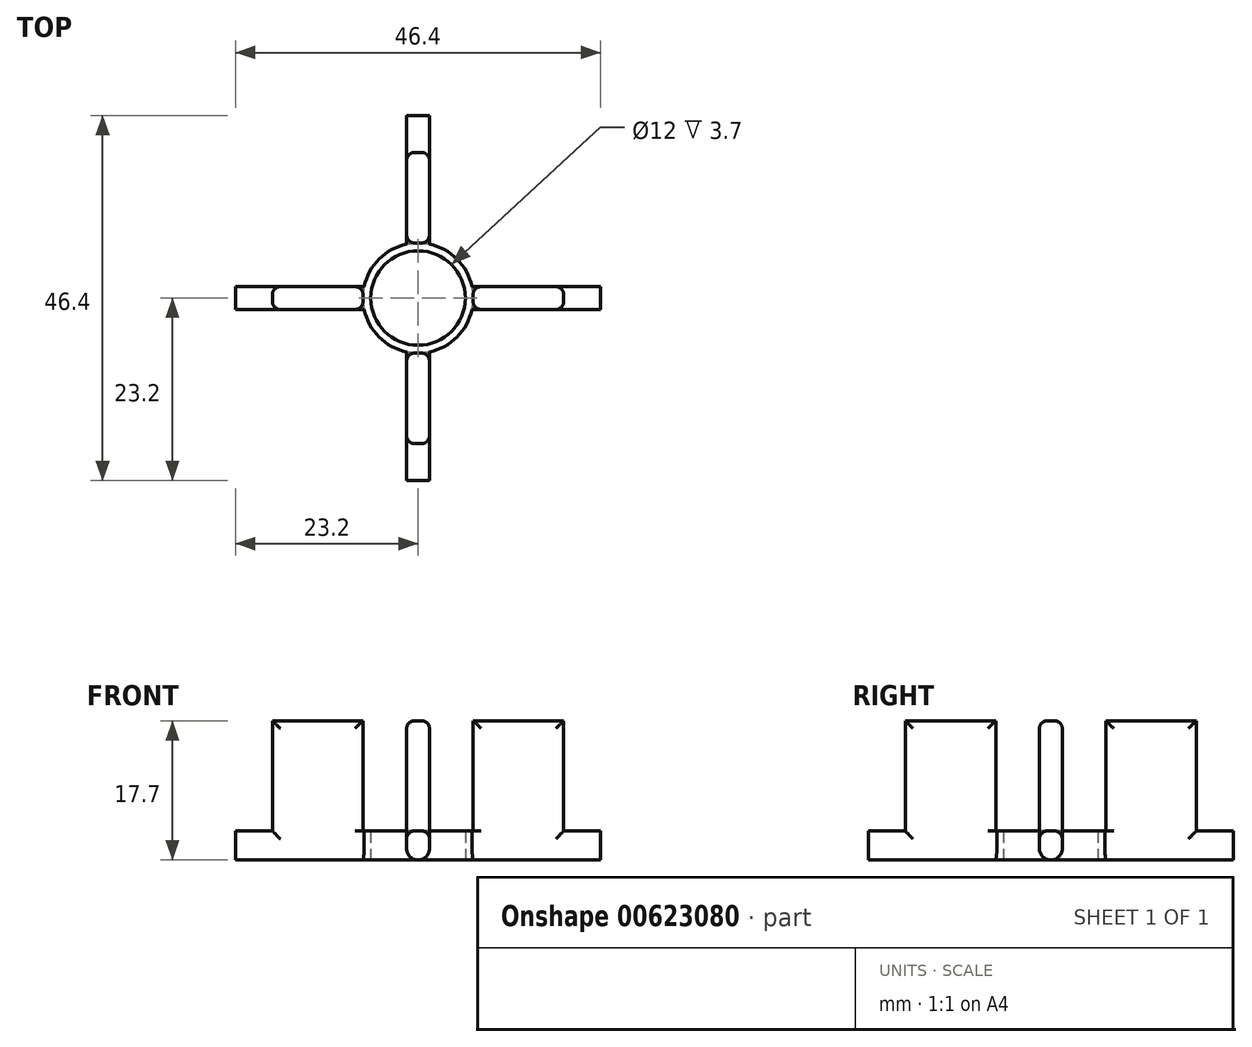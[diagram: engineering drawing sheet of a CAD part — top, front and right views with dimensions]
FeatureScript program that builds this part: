
annotation { "Feature Type Name" : "Feature", "Feature Type Description" : "" }
export const myFeature = defineFeature(function(context is Context, id is Id, definition is map)
    precondition{}
    {
        {
            var Q0;
            Q0=qCreatedBy(makeId("Top.planeOp"),FACE);
            var sketch = newSketch(context, id + "F0", { "sketchPlane" : qUnion([Q0])});
            skCircle(sketch, "E0", {"center": v(0, 0) * mm, "radius": 6 * mm});
            skCircle(sketch, "E1", {"center": v(0, 0) * mm, "radius": 7 * mm});
            skLineSegment(sketch, "E2", {"start": v(-7, 0) * mm, "end": v(-23.2, 0) * mm});
            skLineSegment(sketch, "E3", {"start": v(-23.2, -1.45) * mm, "end": v(-6.85, -1.45) * mm});
            skLineSegment(sketch, "E4", {"start": v(-23.2, -1.45) * mm, "end": v(-23.2, 1.45) * mm});
            skLineSegment(sketch, "E5", {"start": v(-23.2, 1.45) * mm, "end": v(-6.85, 1.45) * mm});
            skLineSegment(sketch, "E6", {"start": v(0, 7) * mm, "end": v(0, 23.2) * mm});
            skLineSegment(sketch, "E7", {"start": v(-1.45, 23.2) * mm, "end": v(-1.45, 6.85) * mm});
            skLineSegment(sketch, "E8", {"start": v(-1.45, 23.2) * mm, "end": v(1.45, 23.2) * mm});
            skLineSegment(sketch, "E9", {"start": v(1.45, 23.2) * mm, "end": v(1.45, 6.85) * mm});
            skLineSegment(sketch, "E10", {"start": v(7, 0) * mm, "end": v(23.2, 0) * mm});
            skLineSegment(sketch, "E11", {"start": v(23.2, 1.45) * mm, "end": v(6.85, 1.45) * mm});
            skLineSegment(sketch, "E12", {"start": v(23.2, 1.45) * mm, "end": v(23.2, -1.45) * mm});
            skLineSegment(sketch, "E13", {"start": v(23.2, -1.45) * mm, "end": v(6.85, -1.45) * mm});
            skLineSegment(sketch, "E14", {"start": v(0, -7) * mm, "end": v(0, -23.2) * mm});
            skLineSegment(sketch, "E15", {"start": v(-1.45, -23.2) * mm, "end": v(-1.45, -6.85) * mm});
            skLineSegment(sketch, "E16", {"start": v(-1.45, -23.2) * mm, "end": v(1.45, -23.2) * mm});
            skLineSegment(sketch, "E17", {"start": v(1.45, -23.2) * mm, "end": v(1.45, -6.85) * mm});
            skSolve(sketch);
        }
        {
            var Q0;
            Q0 = qSketchRegion(id + "F0", true);
            extrude(context, id + "F1", {"entities" : qUnion([Q0]), "depth" : 3.7 * mm, "offsetDistance" : 25 * mm});
        }
        {
            var Q0;
            Q0=makeQuery(id+"F1.opExtrude","CAP_EDGE",EDGE,{"disambiguationData":[OSD([sQuery(id+"F0.wireOp",EDGE,"E9")])],"isStart":true});
            var Q1;
            Q1=makeQuery(id+"F1.opExtrude","CAP_EDGE",EDGE,{"disambiguationData":[OSD([sQuery(id+"F0.wireOp",EDGE,"E11")])],"isStart":true});
            var Q2;
            Q2=makeQuery(id+"F1.opExtrude","CAP_EDGE",EDGE,{"disambiguationData":[OSD([sQuery(id+"F0.wireOp",EDGE,"E13")])],"isStart":true});
            var Q3;
            Q3=makeQuery(id+"F1.opExtrude","CAP_EDGE",EDGE,{"disambiguationData":[OSD([sQuery(id+"F0.wireOp",EDGE,"E17")])],"isStart":true});
            var Q4;
            Q4=makeQuery(id+"F1.opExtrude","CAP_EDGE",EDGE,{"disambiguationData":[OSD([sQuery(id+"F0.wireOp",EDGE,"E15")])],"isStart":true});
            var Q5;
            Q5=makeQuery(id+"F1.opExtrude","CAP_EDGE",EDGE,{"disambiguationData":[OSD([sQuery(id+"F0.wireOp",EDGE,"E3")])],"isStart":true});
            var Q6;
            Q6=makeQuery(id+"F1.opExtrude","CAP_EDGE",EDGE,{"disambiguationData":[OSD([sQuery(id+"F0.wireOp",EDGE,"E5")])],"isStart":true});
            var Q7;
            Q7=makeQuery(id+"F1.opExtrude","CAP_EDGE",EDGE,{"disambiguationData":[OSD([sQuery(id+"F0.wireOp",EDGE,"E7")])],"isStart":true});
            fillet(context, id + "F2", {"entities" : qUnion([Q0, Q1, Q2, Q3, Q4, Q5, Q6, Q7]), "radius" : 1.45 * mm, "tangentPropagation" : true, "allowEdgeOverflow" : false});
        }
        {
            var Q0;
            Q0=makeQuery(id+"F1.opExtrude","CAP_FACE",FACE,{"disambiguationData":[OSD([sQuery(id+"F0.wireOp",EDGE,"E0"),sQuery(id+"F0.wireOp",EDGE,"E1"),sQuery(id+"F0.wireOp",EDGE,"E3"),sQuery(id+"F0.wireOp",EDGE,"E4"),sQuery(id+"F0.wireOp",EDGE,"E5"),sQuery(id+"F0.wireOp",EDGE,"E7"),sQuery(id+"F0.wireOp",EDGE,"E8"),sQuery(id+"F0.wireOp",EDGE,"E9"),sQuery(id+"F0.wireOp",EDGE,"E11"),sQuery(id+"F0.wireOp",EDGE,"E12"),sQuery(id+"F0.wireOp",EDGE,"E13"),sQuery(id+"F0.wireOp",EDGE,"E15"),sQuery(id+"F0.wireOp",EDGE,"E16"),sQuery(id+"F0.wireOp",EDGE,"E17")])],"isStart":false});
            var sketch = newSketch(context, id + "F3", { "sketchPlane" : qUnion([Q0])});
            skArc(sketch, "E18", {"start": v(18.44, -1.45) * mm, "mid": v(18.5, 0) * mm, "end": v(18.44, 1.45) * mm});
            skLineSegment(sketch, "E19.bottom", {"start": v(18.44, -1.45) * mm, "end": v(6.85, -1.45) * mm});
            skLineSegment(sketch, "E19.top", {"start": v(18.44, 1.45) * mm, "end": v(6.85, 1.45) * mm});
            skLineSegment(sketch, "E19.left", {"start": v(18.44, -1.45) * mm, "end": v(18.44, 1.45) * mm});
            skLineSegment(sketch, "E19.right", {"start": v(-18.44, -1.45) * mm, "end": v(-18.44, 1.45) * mm});
            skLineSegment(sketch, "E20.bottom", {"start": v(1.45, -18.44) * mm, "end": v(-1.45, -18.44) * mm});
            skLineSegment(sketch, "E20.top", {"start": v(1.45, 18.44) * mm, "end": v(-1.45, 18.44) * mm});
            skLineSegment(sketch, "E20.left", {"start": v(1.45, -18.44) * mm, "end": v(1.45, -6.85) * mm});
            skLineSegment(sketch, "E20.right", {"start": v(-1.45, -18.44) * mm, "end": v(-1.45, -6.85) * mm});
            skLineSegment(sketch, "E21.trimOffspring", {"start": v(-6.85, -1.45) * mm, "end": v(-18.44, -1.45) * mm});
            skLineSegment(sketch, "E22.trimOffspring", {"start": v(1.45, 6.85) * mm, "end": v(1.45, 18.44) * mm});
            skLineSegment(sketch, "E23.trimOffspring", {"start": v(-1.45, 6.85) * mm, "end": v(-1.45, 18.44) * mm});
            skLineSegment(sketch, "E24.trimOffspring", {"start": v(-6.85, 1.45) * mm, "end": v(-18.44, 1.45) * mm});
            skArc(sketch, "E25.trimOffspring", {"start": v(-1.45, -18.44) * mm, "mid": v(0, -18.5) * mm, "end": v(1.45, -18.44) * mm});
            skArc(sketch, "E26.trimOffspring", {"start": v(-18.44, 1.45) * mm, "mid": v(-18.5, 0) * mm, "end": v(-18.44, -1.45) * mm});
            skArc(sketch, "E27.trimOffspring", {"start": v(1.45, 18.44) * mm, "mid": v(0, 18.5) * mm, "end": v(-1.45, 18.44) * mm});
            skArc(sketch, "E28", {"start": v(-1.45, -6.85) * mm, "mid": v(0, -7) * mm, "end": v(1.45, -6.85) * mm});
            skArc(sketch, "E29.trimOffspring", {"start": v(-6.85, 1.45) * mm, "mid": v(-7, 0) * mm, "end": v(-6.85, -1.45) * mm});
            skArc(sketch, "E30.trimOffspring", {"start": v(1.45, 6.85) * mm, "mid": v(0, 7) * mm, "end": v(-1.45, 6.85) * mm});
            skArc(sketch, "E31.trimOffspring", {"start": v(6.85, -1.45) * mm, "mid": v(7, 0) * mm, "end": v(6.85, 1.45) * mm});
            skSolve(sketch);
        }
        {
            var Q0;
            Q0 = qSketchRegion(id + "F3", true);
            extrude(context, id + "F4", {"entities" : qUnion([Q0]), "operationType" : NewBodyOperationType.ADD, "depth" : 14 * mm, "offsetDistance" : 25 * mm});
        }
        {
            var Q0;
            Q0=makeQuery(id+"F4.opExtrude","CAP_EDGE",EDGE,{"disambiguationData":[OSD([sQuery(id+"F3.wireOp",EDGE,"E19.top")])],"isStart":false});
            var Q1;
            Q1=makeQuery(id+"F4.opExtrude","SWEPT_EDGE",EDGE,{"disambiguationData":[OSD([sQuery(id+"F0.wireOp",EDGE,"E11"),sQuery(id+"F3.wireOp",EDGE,"E18"),sQuery(id+"F3.wireOp",EDGE,"E19.top"),sQuery(id+"F3.wireOp",EDGE,"E19.left")])]});
            var Q2;
            Q2=makeQuery(id+"F1.opExtrude","CAP_EDGE",EDGE,{"disambiguationData":[OSD([sQuery(id+"F0.wireOp",EDGE,"E11")])],"isStart":false});
            var Q3;
            Q3=makeQuery(id+"F1.opExtrude","CAP_EDGE",EDGE,{"disambiguationData":[OSD([sQuery(id+"F0.wireOp",EDGE,"E13")])],"isStart":false});
            var Q4;
            Q4=makeQuery(id+"F4.opExtrude","SWEPT_EDGE",EDGE,{"disambiguationData":[OSD([sQuery(id+"F0.wireOp",EDGE,"E13"),sQuery(id+"F3.wireOp",EDGE,"E18"),sQuery(id+"F3.wireOp",EDGE,"E19.bottom"),sQuery(id+"F3.wireOp",EDGE,"E19.left")])]});
            var Q5;
            Q5=makeQuery(id+"F4.opExtrude","CAP_EDGE",EDGE,{"disambiguationData":[OSD([sQuery(id+"F3.wireOp",EDGE,"E19.bottom")])],"isStart":false});
            var Q6;
            Q6=makeQuery(id+"F4.opExtrude","CAP_EDGE",EDGE,{"disambiguationData":[OSD([sQuery(id+"F3.wireOp",EDGE,"E22.trimOffspring")])],"isStart":false});
            var Q7;
            Q7=makeQuery(id+"F4.opExtrude","CAP_EDGE",EDGE,{"disambiguationData":[OSD([sQuery(id+"F3.wireOp",EDGE,"E23.trimOffspring")])],"isStart":false});
            var Q8;
            Q8=makeQuery(id+"F4.opExtrude","SWEPT_EDGE",EDGE,{"disambiguationData":[OSD([sQuery(id+"F0.wireOp",EDGE,"E9"),sQuery(id+"F3.wireOp",EDGE,"E20.top"),sQuery(id+"F3.wireOp",EDGE,"E22.trimOffspring"),sQuery(id+"F3.wireOp",EDGE,"E27.trimOffspring")])]});
            var Q9;
            Q9=makeQuery(id+"F4.opExtrude","SWEPT_EDGE",EDGE,{"disambiguationData":[OSD([sQuery(id+"F0.wireOp",EDGE,"E7"),sQuery(id+"F3.wireOp",EDGE,"E20.top"),sQuery(id+"F3.wireOp",EDGE,"E23.trimOffspring"),sQuery(id+"F3.wireOp",EDGE,"E27.trimOffspring")])]});
            var Q10;
            Q10=makeQuery(id+"F1.opExtrude","CAP_EDGE",EDGE,{"disambiguationData":[OSD([sQuery(id+"F0.wireOp",EDGE,"E9")])],"isStart":false});
            var Q11;
            Q11=makeQuery(id+"F1.opExtrude","CAP_EDGE",EDGE,{"disambiguationData":[OSD([sQuery(id+"F0.wireOp",EDGE,"E7")])],"isStart":false});
            var Q12;
            Q12=makeQuery(id+"F4.opExtrude","CAP_EDGE",EDGE,{"disambiguationData":[OSD([sQuery(id+"F3.wireOp",EDGE,"E27.trimOffspring")])],"isStart":true});
            var Q13;
            Q13=makeQuery(id+"F4.opExtrude","SWEPT_EDGE",EDGE,{"disambiguationData":[OSD([sQuery(id+"F0.wireOp",EDGE,"E5"),sQuery(id+"F3.wireOp",EDGE,"E19.right"),sQuery(id+"F3.wireOp",EDGE,"E24.trimOffspring"),sQuery(id+"F3.wireOp",EDGE,"E26.trimOffspring")])]});
            var Q14;
            Q14=makeQuery(id+"F4.opExtrude","SWEPT_EDGE",EDGE,{"disambiguationData":[OSD([sQuery(id+"F0.wireOp",EDGE,"E3"),sQuery(id+"F3.wireOp",EDGE,"E19.right"),sQuery(id+"F3.wireOp",EDGE,"E21.trimOffspring"),sQuery(id+"F3.wireOp",EDGE,"E26.trimOffspring")])]});
            var Q15;
            Q15=makeQuery(id+"F1.opExtrude","CAP_EDGE",EDGE,{"disambiguationData":[OSD([sQuery(id+"F0.wireOp",EDGE,"E5")])],"isStart":false});
            var Q16;
            Q16=makeQuery(id+"F4.opExtrude","SWEPT_EDGE",EDGE,{"disambiguationData":[OSD([sQuery(id+"F0.wireOp",EDGE,"E15"),sQuery(id+"F3.wireOp",EDGE,"E20.bottom"),sQuery(id+"F3.wireOp",EDGE,"E20.right"),sQuery(id+"F3.wireOp",EDGE,"E25.trimOffspring")])]});
            var Q17;
            Q17=makeQuery(id+"F4.opExtrude","SWEPT_EDGE",EDGE,{"disambiguationData":[OSD([sQuery(id+"F0.wireOp",EDGE,"E17"),sQuery(id+"F3.wireOp",EDGE,"E20.bottom"),sQuery(id+"F3.wireOp",EDGE,"E20.left"),sQuery(id+"F3.wireOp",EDGE,"E25.trimOffspring")])]});
            var Q18;
            Q18=makeQuery(id+"F1.opExtrude","CAP_EDGE",EDGE,{"disambiguationData":[OSD([sQuery(id+"F0.wireOp",EDGE,"E15")])],"isStart":false});
            var Q19;
            Q19=makeQuery(id+"F1.opExtrude","CAP_EDGE",EDGE,{"disambiguationData":[OSD([sQuery(id+"F0.wireOp",EDGE,"E17")])],"isStart":false});
            var Q20;
            Q20=makeQuery(id+"F1.opExtrude","CAP_EDGE",EDGE,{"disambiguationData":[OSD([sQuery(id+"F0.wireOp",EDGE,"E3")])],"isStart":false});
            var Q21;
            Q21=makeQuery(id+"F4.opExtrude","CAP_EDGE",EDGE,{"disambiguationData":[OSD([sQuery(id+"F3.wireOp",EDGE,"E24.trimOffspring")])],"isStart":false});
            var Q22;
            Q22=makeQuery(id+"F4.opExtrude","CAP_EDGE",EDGE,{"disambiguationData":[OSD([sQuery(id+"F3.wireOp",EDGE,"E21.trimOffspring")])],"isStart":false});
            var Q23;
            Q23=makeQuery(id+"F4.opExtrude","CAP_EDGE",EDGE,{"disambiguationData":[OSD([sQuery(id+"F3.wireOp",EDGE,"E20.right")])],"isStart":false});
            var Q24;
            Q24=makeQuery(id+"F4.opExtrude","CAP_EDGE",EDGE,{"disambiguationData":[OSD([sQuery(id+"F3.wireOp",EDGE,"E20.left")])],"isStart":false});
            var Q25;
            Q25=makeQuery(id+"F4.opExtrude","SWEPT_EDGE",EDGE,{"disambiguationData":[OSD([sQuery(id+"F0.wireOp",EDGE,"E1"),sQuery(id+"F3.wireOp",EDGE,"E20.right"),sQuery(id+"F3.wireOp",EDGE,"E28")])]});
            var Q26;
            Q26=makeQuery(id+"F4.opExtrude","SWEPT_EDGE",EDGE,{"disambiguationData":[OSD([sQuery(id+"F0.wireOp",EDGE,"E1"),sQuery(id+"F3.wireOp",EDGE,"E20.left"),sQuery(id+"F3.wireOp",EDGE,"E28")])]});
            var Q27;
            Q27=makeQuery(id+"F4.opExtrude","SWEPT_EDGE",EDGE,{"disambiguationData":[OSD([sQuery(id+"F0.wireOp",EDGE,"E1"),sQuery(id+"F3.wireOp",EDGE,"E19.bottom"),sQuery(id+"F3.wireOp",EDGE,"E31.trimOffspring")])]});
            var Q28;
            Q28=makeQuery(id+"F4.opExtrude","SWEPT_EDGE",EDGE,{"disambiguationData":[OSD([sQuery(id+"F0.wireOp",EDGE,"E1"),sQuery(id+"F3.wireOp",EDGE,"E19.top"),sQuery(id+"F3.wireOp",EDGE,"E31.trimOffspring")])]});
            var Q29;
            Q29=makeQuery(id+"F4.opExtrude","SWEPT_EDGE",EDGE,{"disambiguationData":[OSD([sQuery(id+"F0.wireOp",EDGE,"E1"),sQuery(id+"F3.wireOp",EDGE,"E22.trimOffspring"),sQuery(id+"F3.wireOp",EDGE,"E30.trimOffspring")])]});
            var Q30;
            Q30=makeQuery(id+"F4.opExtrude","SWEPT_EDGE",EDGE,{"disambiguationData":[OSD([sQuery(id+"F0.wireOp",EDGE,"E1"),sQuery(id+"F3.wireOp",EDGE,"E23.trimOffspring"),sQuery(id+"F3.wireOp",EDGE,"E30.trimOffspring")])]});
            var Q31;
            Q31=makeQuery(id+"F4.opExtrude","SWEPT_EDGE",EDGE,{"disambiguationData":[OSD([sQuery(id+"F0.wireOp",EDGE,"E1"),sQuery(id+"F3.wireOp",EDGE,"E24.trimOffspring"),sQuery(id+"F3.wireOp",EDGE,"E29.trimOffspring")])]});
            var Q32;
            Q32=makeQuery(id+"F4.opExtrude","SWEPT_EDGE",EDGE,{"disambiguationData":[OSD([sQuery(id+"F0.wireOp",EDGE,"E1"),sQuery(id+"F3.wireOp",EDGE,"E21.trimOffspring"),sQuery(id+"F3.wireOp",EDGE,"E29.trimOffspring")])]});
            fillet(context, id + "F5", {"entities" : qUnion([Q0, Q1, Q2, Q3, Q4, Q5, Q6, Q7, Q8, Q9, Q10, Q11, Q12, Q13, Q14, Q15, Q16, Q17, Q18, Q19, Q20, Q21, Q22, Q23, Q24, Q25, Q26, Q27, Q28, Q29, Q30, Q31, Q32]), "radius" : 1 * mm, "tangentPropagation" : true, "allowEdgeOverflow" : false});
        }
    });
